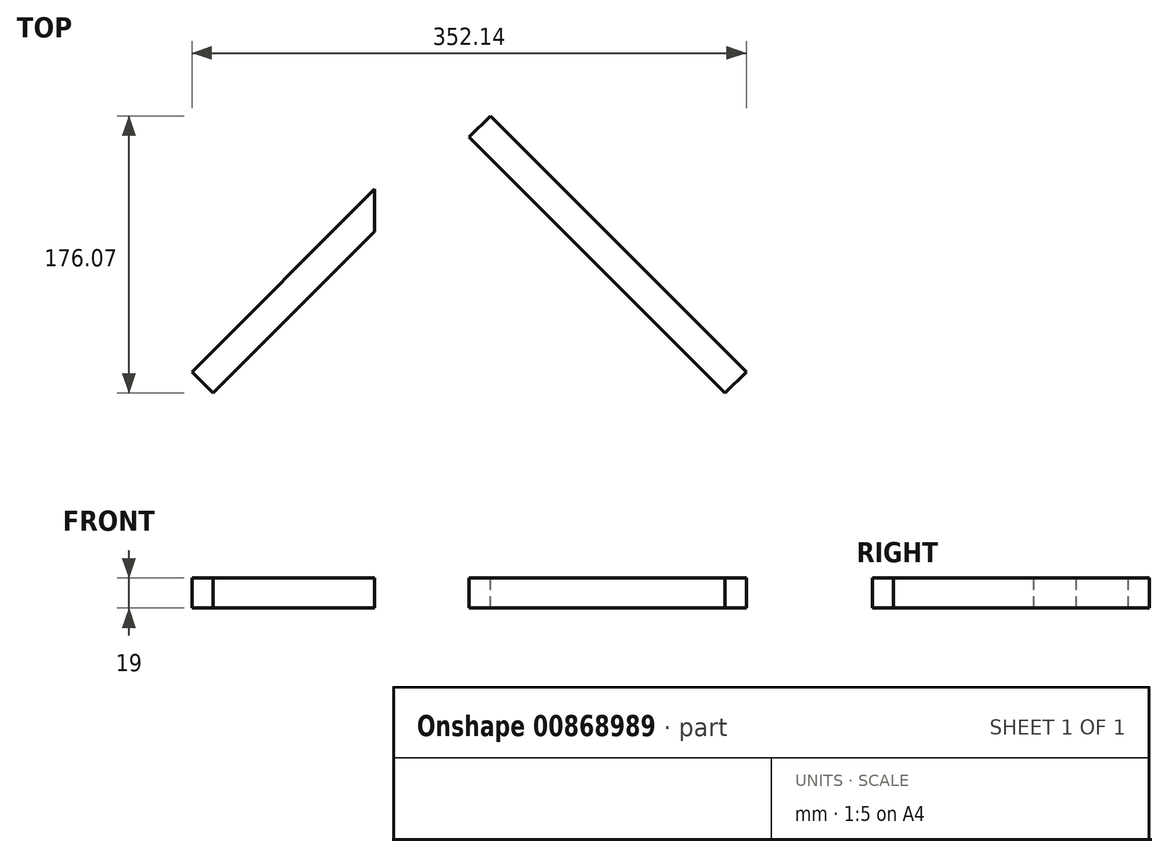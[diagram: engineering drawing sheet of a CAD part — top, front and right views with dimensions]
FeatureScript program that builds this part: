
annotation { "Feature Type Name" : "Feature", "Feature Type Description" : "" }
export const myFeature = defineFeature(function(context is Context, id is Id, definition is map)
    precondition{}
    {
        {
            var Q0;
            Q0=qCreatedBy(makeId("Top.planeOp"),FACE);
            var sketch = newSketch(context, id + "F0", { "sketchPlane" : qUnion([Q0])});
            skLineSegment(sketch, "E0.bottom", {"start": v(0, 0) * mm, "end": v(-400, 0) * mm, "construction": true});
            skLineSegment(sketch, "E0.top", {"start": v(0, -89) * mm, "end": v(-400, -89) * mm, "construction": true});
            skLineSegment(sketch, "E0.left", {"start": v(0, 0) * mm, "end": v(0, -89) * mm, "construction": true});
            skLineSegment(sketch, "E0.right", {"start": v(-400, 0) * mm, "end": v(-400, -89) * mm, "construction": true});
            skLineSegment(sketch, "E1", {"start": v(-400, 0) * mm, "end": v(-400, -9) * mm, "construction": true});
            skLineSegment(sketch, "E2", {"start": v(-400, -89) * mm, "end": v(-400, -80) * mm, "construction": true});
            skPoint(sketch, "E3", {"position": v(-400, -9) * mm});
            skPoint(sketch, "E4", {"position": v(-400, -80) * mm});
            skLineSegment(sketch, "E5", {"start": v(-400, -9) * mm, "end": v(0, -9) * mm, "construction": true});
            skLineSegment(sketch, "E6", {"start": v(-400, -80) * mm, "end": v(0, -80) * mm, "construction": true});
            skPoint(sketch, "E7", {"position": v(-200, 0) * mm});
            skLineSegment(sketch, "E8", {"start": v(-200, 0) * mm, "end": v(-200, -89) * mm, "construction": true});
            skLineSegment(sketch, "E9", {"start": v(-200, 0) * mm, "end": v(-181, 0) * mm, "construction": true});
            skLineSegment(sketch, "E10", {"start": v(-181, 0) * mm, "end": v(-181, 19) * mm, "construction": true});
            skLineSegment(sketch, "E11", {"start": v(-200, 0) * mm, "end": v(-219, 0) * mm, "construction": true});
            skLineSegment(sketch, "E12", {"start": v(-219, 0) * mm, "end": v(-219, 19) * mm, "construction": true});
            skLineSegment(sketch, "E13", {"start": v(-200, 0) * mm, "end": v(-219, 19) * mm, "construction": true});
            skLineSegment(sketch, "E14", {"start": v(-200, 0) * mm, "end": v(-181, 19) * mm, "construction": true});
            skLineSegment(sketch, "E15", {"start": v(-200, 0) * mm, "end": v(-213.44, 13.44) * mm, "construction": true});
            skLineSegment(sketch, "E16", {"start": v(-213.44, 13.44) * mm, "end": v(-186.56, 13.44) * mm, "construction": true});
            skPoint(sketch, "E17", {"position": v(-213.44, 13.44) * mm});
            skPoint(sketch, "E18", {"position": v(-186.56, 13.44) * mm});
            skLineSegment(sketch, "E19", {"start": v(-213.44, 13.44) * mm, "end": v(-376.07, -149.2) * mm, "construction": true});
            skLineSegment(sketch, "E20", {"start": v(-200, 0) * mm, "end": v(-362.63, -162.63) * mm, "construction": true});
            skLineSegment(sketch, "E21", {"start": v(-200, 0) * mm, "end": v(-37.37, -162.63) * mm, "construction": true});
            skLineSegment(sketch, "E22", {"start": v(-186.56, 13.44) * mm, "end": v(-23.93, -149.2) * mm, "construction": true});
            skLineSegment(sketch, "E23", {"start": v(-376.07, -149.2) * mm, "end": v(-362.63, -162.63) * mm});
            skLineSegment(sketch, "E24", {"start": v(-200, 0) * mm, "end": v(-213.44, 13.44) * mm});
            skLineSegment(sketch, "E25", {"start": v(-213.44, 13.44) * mm, "end": v(-376.07, -149.2) * mm});
            skLineSegment(sketch, "E26", {"start": v(-362.63, -162.63) * mm, "end": v(-200, 0) * mm});
            skLineSegment(sketch, "E27", {"start": v(-200, 0) * mm, "end": v(-37.37, -162.63) * mm});
            skLineSegment(sketch, "E28", {"start": v(-37.37, -162.63) * mm, "end": v(-23.93, -149.2) * mm});
            skLineSegment(sketch, "E29", {"start": v(-23.93, -149.2) * mm, "end": v(-186.56, 13.44) * mm});
            skLineSegment(sketch, "E30", {"start": v(-186.56, 13.44) * mm, "end": v(-200, 0) * mm});
            skLineSegment(sketch, "E31", {"start": v(-400, 0) * mm, "end": v(-391, 0) * mm, "construction": true});
            skLineSegment(sketch, "E32", {"start": v(-391, 0) * mm, "end": v(-391, -89) * mm, "construction": true});
            skLineSegment(sketch, "E33", {"start": v(0, 0) * mm, "end": v(-9, 0) * mm, "construction": true});
            skLineSegment(sketch, "E34", {"start": v(-9, 0) * mm, "end": v(-9, -89) * mm, "construction": true});
            skPoint(sketch, "E35", {"position": v(-391, -9) * mm});
            skPoint(sketch, "E36", {"position": v(-391, -80) * mm});
            skPoint(sketch, "E37", {"position": v(-391, -89) * mm});
            skPoint(sketch, "E38", {"position": v(-9, -89) * mm});
            skPoint(sketch, "E39", {"position": v(-9, -80) * mm});
            skPoint(sketch, "E40", {"position": v(-9, -9) * mm});
            skPoint(sketch, "E41", {"position": v(-200, -9) * mm});
            skPoint(sketch, "E42", {"position": v(-200, -80) * mm});
            skCircle(sketch, "E43", {"center": v(-391, -9) * mm, "radius": 5 * mm, "construction": true});
            skCircle(sketch, "E44", {"center": v(-391, -80) * mm, "radius": 5 * mm, "construction": true});
            skCircle(sketch, "E45", {"center": v(-200, -80) * mm, "radius": 5 * mm, "construction": true});
            skCircle(sketch, "E46", {"center": v(-200, -9) * mm, "radius": 5 * mm, "construction": true});
            skCircle(sketch, "E47", {"center": v(-9, -9) * mm, "radius": 5 * mm, "construction": true});
            skCircle(sketch, "E48", {"center": v(-9, -80) * mm, "radius": 5 * mm, "construction": true});
            skLineSegment(sketch, "E49", {"start": v(-400, -89) * mm, "end": v(-400, -44.5) * mm, "construction": true});
            skLineSegment(sketch, "E50", {"start": v(-400, -44.5) * mm, "end": v(-400, -66.5) * mm, "construction": true});
            skLineSegment(sketch, "E51", {"start": v(-400, -44.5) * mm, "end": v(-400, -22.5) * mm, "construction": true});
            skPoint(sketch, "E52.oppositeSnap0", {"position": v(-400, -66.75) * mm});
            skLineSegment(sketch, "E52.left", {"start": v(-400, -22.5) * mm, "end": v(-400, -66.75) * mm});
            skLineSegment(sketch, "E53", {"start": v(-140, -22.5) * mm, "end": v(-260, -22.5) * mm, "construction": true});
            skLineSegment(sketch, "E54", {"start": v(-260, -22.5) * mm, "end": v(-260, -66.75) * mm, "construction": true});
            skLineSegment(sketch, "E55", {"start": v(-260, -66.75) * mm, "end": v(-140, -66.75) * mm, "construction": true});
            skLineSegment(sketch, "E56", {"start": v(-140, -66.75) * mm, "end": v(-140, -22.5) * mm, "construction": true});
            skLineSegment(sketch, "E57.bottom", {"start": v(-260, -22.5) * mm, "end": v(-140, -22.5) * mm});
            skLineSegment(sketch, "E57.top", {"start": v(-260, -66.75) * mm, "end": v(-140, -66.75) * mm});
            skLineSegment(sketch, "E57.left", {"start": v(-260, -22.5) * mm, "end": v(-260, -66.75) * mm});
            skLineSegment(sketch, "E57.right", {"start": v(-140, -22.5) * mm, "end": v(-140, -66.75) * mm});
            skLineSegment(sketch, "E58", {"start": v(-260, -22.5) * mm, "end": v(-241.22, -22.5) * mm, "construction": true});
            skLineSegment(sketch, "E59", {"start": v(-235.86, -8.99) * mm, "end": v(-209, -9) * mm, "construction": true});
            skLineSegment(sketch, "E60", {"start": v(-235.86, -8.99) * mm, "end": v(-222.43, -9) * mm, "construction": true});
            skSolve(sketch);
        }
        {
            var Q0;
            Q0=makeQuery(id+"F0.imprint","IMPRINT",FACE,{"disambiguationData":[TD([[makeQuery(id+"F0.imprint","IMPRINT",EDGE,{"derivedFrom":sQuery(id+"F0.wireOp",EDGE,"E23")}),1.0]])]});
            var Q1;
            Q1=makeQuery(id+"F0.imprint","IMPRINT",FACE,{"disambiguationData":[TD([[makeQuery(id+"F0.imprint","IMPRINT",EDGE,{"derivedFrom":sQuery(id+"F0.wireOp",EDGE,"E27")}),1.0]])]});
            extrude(context, id + "F1", {"entities" : qUnion([Q0, Q1]), "oppositeDirection" : true, "depth" : 19 * mm, "offsetDistance" : 25 * mm});
        }
    });
